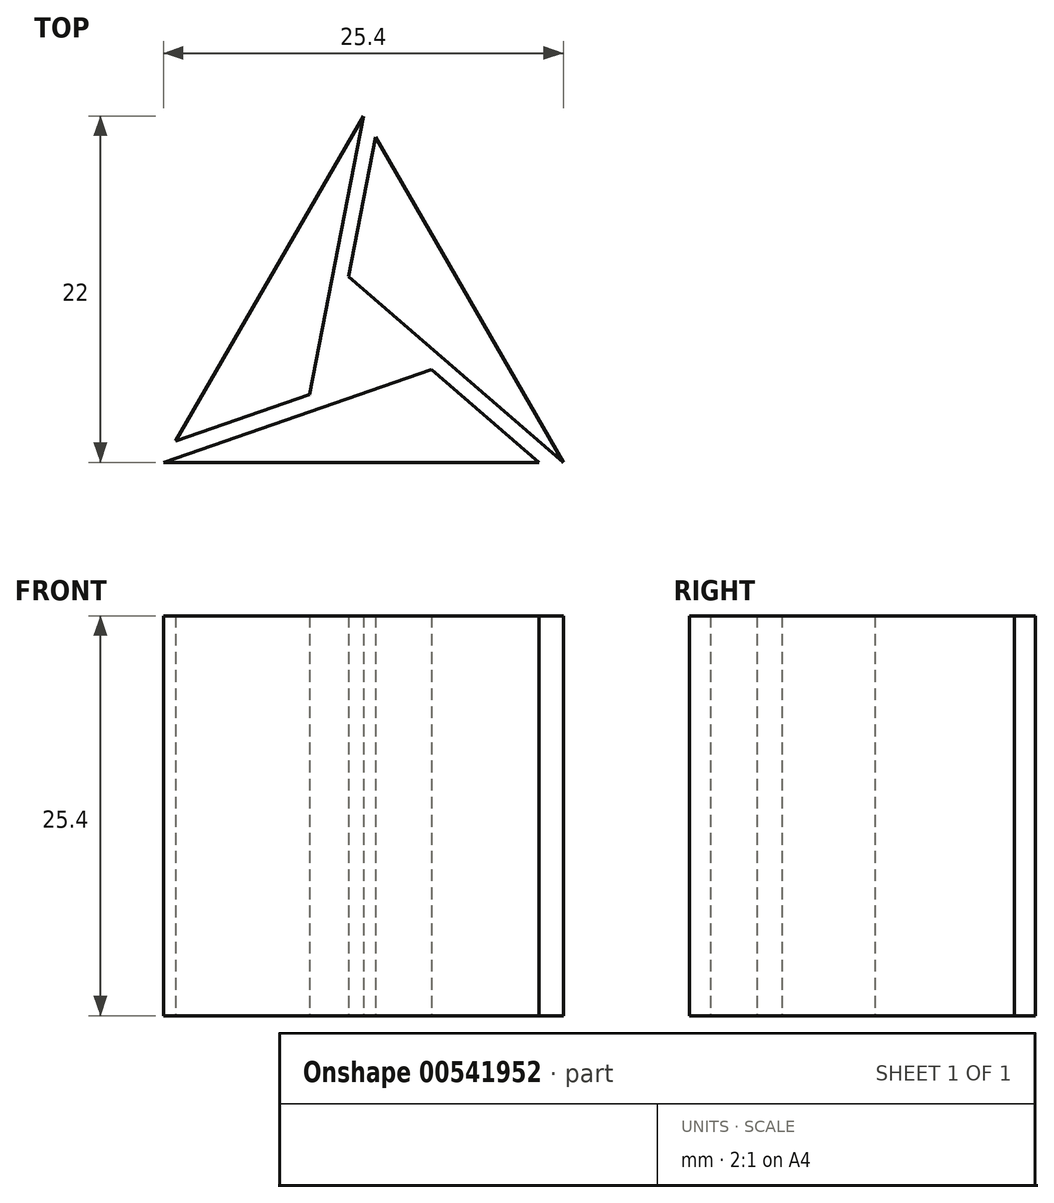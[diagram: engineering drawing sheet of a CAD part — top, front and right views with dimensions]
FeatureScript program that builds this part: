
annotation { "Feature Type Name" : "Feature", "Feature Type Description" : "" }
export const myFeature = defineFeature(function(context is Context, id is Id, definition is map)
    precondition{}
    {
        {
            var Q0;
            Q0=qCreatedBy(makeId("Top.planeOp"),FACE);
            var sketch = newSketch(context, id + "F0", { "sketchPlane" : qUnion([Q0])});
            skLineSegment(sketch, "E0", {"start": v(0, 0) * mm, "end": v(25.4, 0) * mm, "construction": true});
            skLineSegment(sketch, "E1", {"start": v(25.4, 0) * mm, "end": v(12.7, 22) * mm, "construction": true});
            skLineSegment(sketch, "E2", {"start": v(12.7, 22) * mm, "end": v(0, 0) * mm, "construction": true});
            skLineSegment(sketch, "E3", {"start": v(25.4, 0) * mm, "end": v(12.7, 7.33) * mm, "construction": true});
            skLineSegment(sketch, "E4", {"start": v(12.7, 22) * mm, "end": v(12.7, 7.33) * mm, "construction": true});
            skLineSegment(sketch, "E5", {"start": v(0, 0) * mm, "end": v(12.7, 7.33) * mm, "construction": true});
            skLineSegment(sketch, "E6", {"start": v(23.85, 0) * mm, "end": v(17.03, 5.9) * mm});
            skLineSegment(sketch, "E7", {"start": v(17.03, 5.9) * mm, "end": v(0, 0) * mm});
            skLineSegment(sketch, "E8", {"start": v(0.78, 1.34) * mm, "end": v(9.3, 4.3) * mm});
            skLineSegment(sketch, "E9", {"start": v(9.3, 4.3) * mm, "end": v(12.7, 22) * mm});
            skLineSegment(sketch, "E10", {"start": v(13.48, 20.65) * mm, "end": v(11.77, 11.8) * mm});
            skLineSegment(sketch, "E11", {"start": v(11.77, 11.8) * mm, "end": v(25.4, 0) * mm});
            skLineSegment(sketch, "E12", {"start": v(0.78, 1.34) * mm, "end": v(12.7, 22) * mm});
            skLineSegment(sketch, "E13", {"start": v(25.4, 0) * mm, "end": v(13.48, 20.65) * mm});
            skLineSegment(sketch, "E14", {"start": v(0, 0) * mm, "end": v(23.85, 0) * mm});
            skPoint(sketch, "E15", {"position": v(8.52, 2.95) * mm});
            skCircle(sketch, "E16", {"center": v(17.03, 5.9) * mm, "radius": 9.01 * mm, "construction": true});
            skSolve(sketch);
        }
        {
            var Q0;
            Q0=makeQuery(id+"F0.imprint","IMPRINT",FACE,{"disambiguationData":[TD([[makeQuery(id+"F0.imprint","IMPRINT",EDGE,{"derivedFrom":sQuery(id+"F0.wireOp",EDGE,"E8")}),1.0]])]});
            var Q1;
            Q1=makeQuery(id+"F0.imprint","IMPRINT",FACE,{"disambiguationData":[TD([[makeQuery(id+"F0.imprint","IMPRINT",EDGE,{"derivedFrom":sQuery(id+"F0.wireOp",EDGE,"E10")}),1.0]])]});
            var Q2;
            Q2=makeQuery(id+"F0.imprint","IMPRINT",FACE,{"disambiguationData":[TD([[makeQuery(id+"F0.imprint","IMPRINT",EDGE,{"derivedFrom":sQuery(id+"F0.wireOp",EDGE,"E6")}),1.0]])]});
            extrude(context, id + "F1", {"entities" : qUnion([Q0, Q1, Q2]), "depth" : 25.4 * mm, "offsetDistance" : 25.4 * mm});
        }
    });
